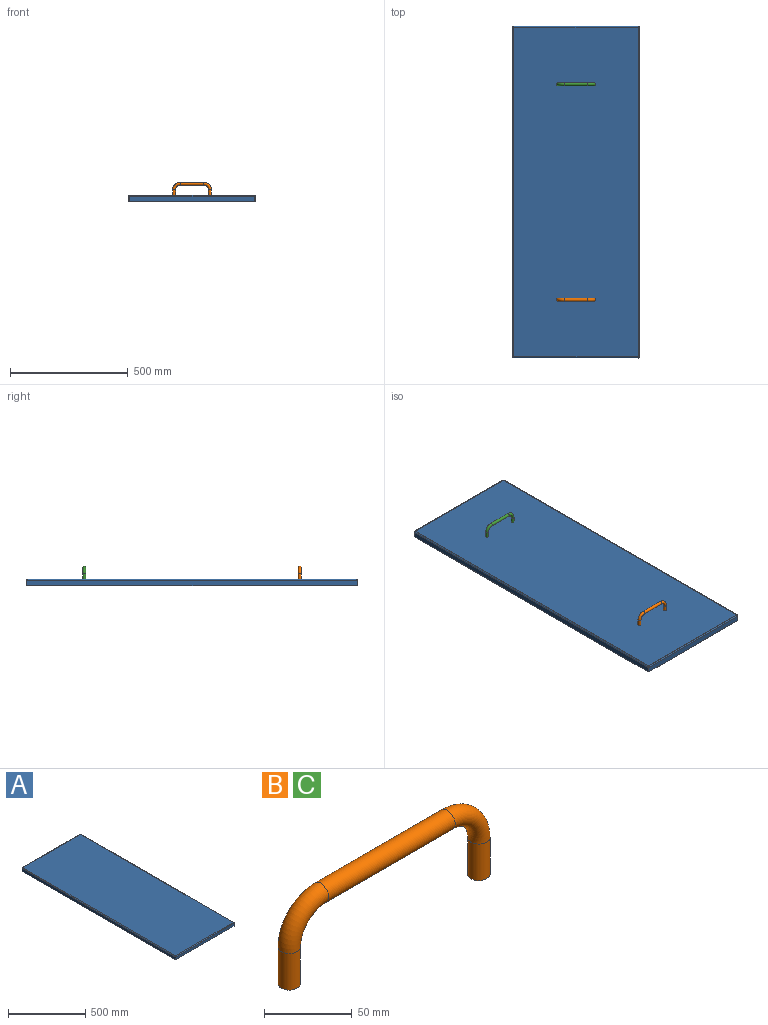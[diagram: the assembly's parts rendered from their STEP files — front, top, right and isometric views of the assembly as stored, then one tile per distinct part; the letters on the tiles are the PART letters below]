
ASSEMBLY  parts=3 mates=1
PART A: 46 faces, bbox 538.7x1408.7x28.1 mm
  f0: plane 2.66x2.26mm, normal (0,0,1), area 6mm2, adj f4,f5,f6,f43
  f1: plane 2.66x2.26mm, normal (0,0,1), area 6mm2, adj f2,f5,f6,f42
  f2: plane 23.11x2.66mm, normal (-1,0,0), area 61.4mm2, adj f1,f3,f5,f6
  f3: plane 533.35x2.66mm, normal (0,0,-1), area 1417mm2, adj f2,f4,f5,f6
  f4: plane 23.11x2.66mm, normal (1,0,0), area 61.4mm2, adj f0,f3,f5,f6
  f5: plane 533.35x23.11mm, normal (0,-1,0), area 12327.8mm2, adj f0,f1,f2,f3,f4,f44
  f6: plane 533.35x23.11mm, normal (0,1,0), area 12327.8mm2, adj f0,f1,f2,f3,f4,f45
  f7: plane 1398.78x528.83mm, normal (0,0,1), area 739713mm2, adj f18,f29,f40,f44
  f8: plane 1398.78x528.83mm, normal (0,0,-1), area 739713mm2, adj f19,f30,f41,f45
  f9: plane 2.66x2.26mm, normal (0,0,1), area 6mm2, adj f13,f14,f15,f16
  f10: plane 2.66x2.26mm, normal (0,0,1), area 6mm2, adj f11,f14,f15,f17
  f11: plane 23.11x2.66mm, normal (1,0,0), area 61.4mm2, adj f10,f12,f14,f15
  f12: plane 533.35x2.66mm, normal (0,0,-1), area 1417mm2, adj f11,f13,f14,f15
  f13: plane 23.11x2.66mm, normal (-1,0,0), area 61.4mm2, adj f9,f12,f14,f15
  f14: plane 533.35x23.11mm, normal (0,1,0), area 12327.8mm2, adj f9,f10,f11,f12,f13,f18
  f15: plane 533.35x23.11mm, normal (0,-1,0), area 12327.8mm2, adj f9,f10,f11,f12,f13,f19
  f16: plane 4.94x4.94mm, normal (-1,0,0), area 15.1mm2, adj f9,f18,f19,f38
  f17: plane 4.94x4.94mm, normal (1,0,0), area 15.1mm2, adj f10,f18,f19,f27
  f18: cylinder r=4.94mm len=528.83mm, axis (-1,0,0), area 4105.9mm2, adj f7,f14,f16,f17
  f19: cylinder r=2.29mm len=528.83mm, axis (-1,0,0), area 1898.9mm2, adj f8,f15,f16,f17
  f20: plane 2.66x2.26mm, normal (0,0,1), area 6mm2, adj f24,f25,f26,f27
  f21: plane 2.66x2.26mm, normal (0,0,1), area 6mm2, adj f22,f25,f26,f28
  f22: plane 23.11x2.66mm, normal (0,-1,0), area 61.4mm2, adj f21,f23,f25,f26
  f23: plane 1403.3x2.66mm, normal (0,0,-1), area 3728.3mm2, adj f22,f24,f25,f26
  f24: plane 23.11x2.66mm, normal (0,1,0), area 61.4mm2, adj f20,f23,f25,f26
  f25: plane 1403.3x23.11mm, normal (1,0,0), area 32435.9mm2, adj f20,f21,f22,f23,f24,f29
  f26: plane 1403.3x23.11mm, normal (-1,0,0), area 32435.9mm2, adj f20,f21,f22,f23,f24,f30
  f27: plane 4.94x4.94mm, normal (0,1,0), area 15.1mm2, adj f17,f20,f29,f30
  f28: plane 4.94x4.94mm, normal (0,-1,0), area 15.1mm2, adj f21,f29,f30,f43
  f29: cylinder r=4.94mm len=1398.78mm, axis (0,1,0), area 10860.4mm2, adj f7,f25,f27,f28
  f30: cylinder r=2.29mm len=1398.78mm, axis (0,1,0), area 5022.8mm2, adj f8,f26,f27,f28
  f31: plane 2.66x2.26mm, normal (0,0,1), area 6mm2, adj f35,f36,f37,f39
  f32: plane 2.66x2.26mm, normal (0,0,1), area 6mm2, adj f33,f36,f37,f38
  f33: plane 23.11x2.66mm, normal (0,1,0), area 61.4mm2, adj f32,f34,f36,f37
  f34: plane 1403.3x2.66mm, normal (0,0,-1), area 3728.3mm2, adj f33,f35,f36,f37
  f35: plane 23.11x2.66mm, normal (0,-1,0), area 61.4mm2, adj f31,f34,f36,f37
  f36: plane 1403.3x23.11mm, normal (-1,0,0), area 32435.9mm2, adj f31,f32,f33,f34,f35,f40
  f37: plane 1403.3x23.11mm, normal (1,0,0), area 32435.9mm2, adj f31,f32,f33,f34,f35,f41
  f38: plane 4.94x4.94mm, normal (0,1,0), area 15.1mm2, adj f16,f32,f40,f41
  f39: plane 4.94x4.94mm, normal (0,-1,0), area 15.1mm2, adj f31,f40,f41,f42
  f40: cylinder r=4.94mm len=1398.78mm, axis (0,1,0), area 10860.4mm2, adj f7,f36,f38,f39
  f41: cylinder r=2.29mm len=1398.78mm, axis (0,1,0), area 5022.8mm2, adj f8,f37,f38,f39
  f42: plane 4.94x4.94mm, normal (-1,0,0), area 15.1mm2, adj f1,f39,f44,f45
  f43: plane 4.94x4.94mm, normal (1,0,0), area 15.1mm2, adj f0,f28,f44,f45
  f44: cylinder r=4.94mm len=528.83mm, axis (-1,0,0), area 4105.9mm2, adj f5,f7,f42,f43
  f45: cylinder r=2.29mm len=528.83mm, axis (-1,0,0), area 1898.9mm2, adj f6,f8,f42,f43
PART B: 7 faces, bbox 170.3x12.7x59.8 mm
  f0: plane 12.7x12.7mm, normal (0,0,-1), area 126.7mm2, adj f1
  f1: cylinder r=6.35mm len=25.4mm, axis (0,0,1), area 1013.4mm2, adj f0,f2
  f2: torus R=25.4mm, axis (0,1,0), area 1591.9mm2, adj f1,f3
  f3: cylinder r=6.35mm len=101.6mm, axis (1,0,0), area 4053.7mm2, adj f2,f6
  f4: plane 12.7x12.7mm, normal (0,0,-1), area 126.7mm2, adj f5
  f5: cylinder r=6.35mm len=25.4mm, axis (0,0,1), area 1013.4mm2, adj f4,f6
  f6: torus R=25.4mm, axis (0,1,0), area 1591.9mm2, adj f3,f5
PART C: same geometry as B
PLACE A t=(544,-604.36,-474.3)mm
PLACE B t=(-233.88,753.94,3056.3)mm
PLACE C rot(axis=(0,0,1),180deg) t=(-233.88,1668.34,3056.3)mm
MATE fastened B.f0 <-> A.f8  axis (0,0,1) through (-233.88,753.94,3056.3)mm
